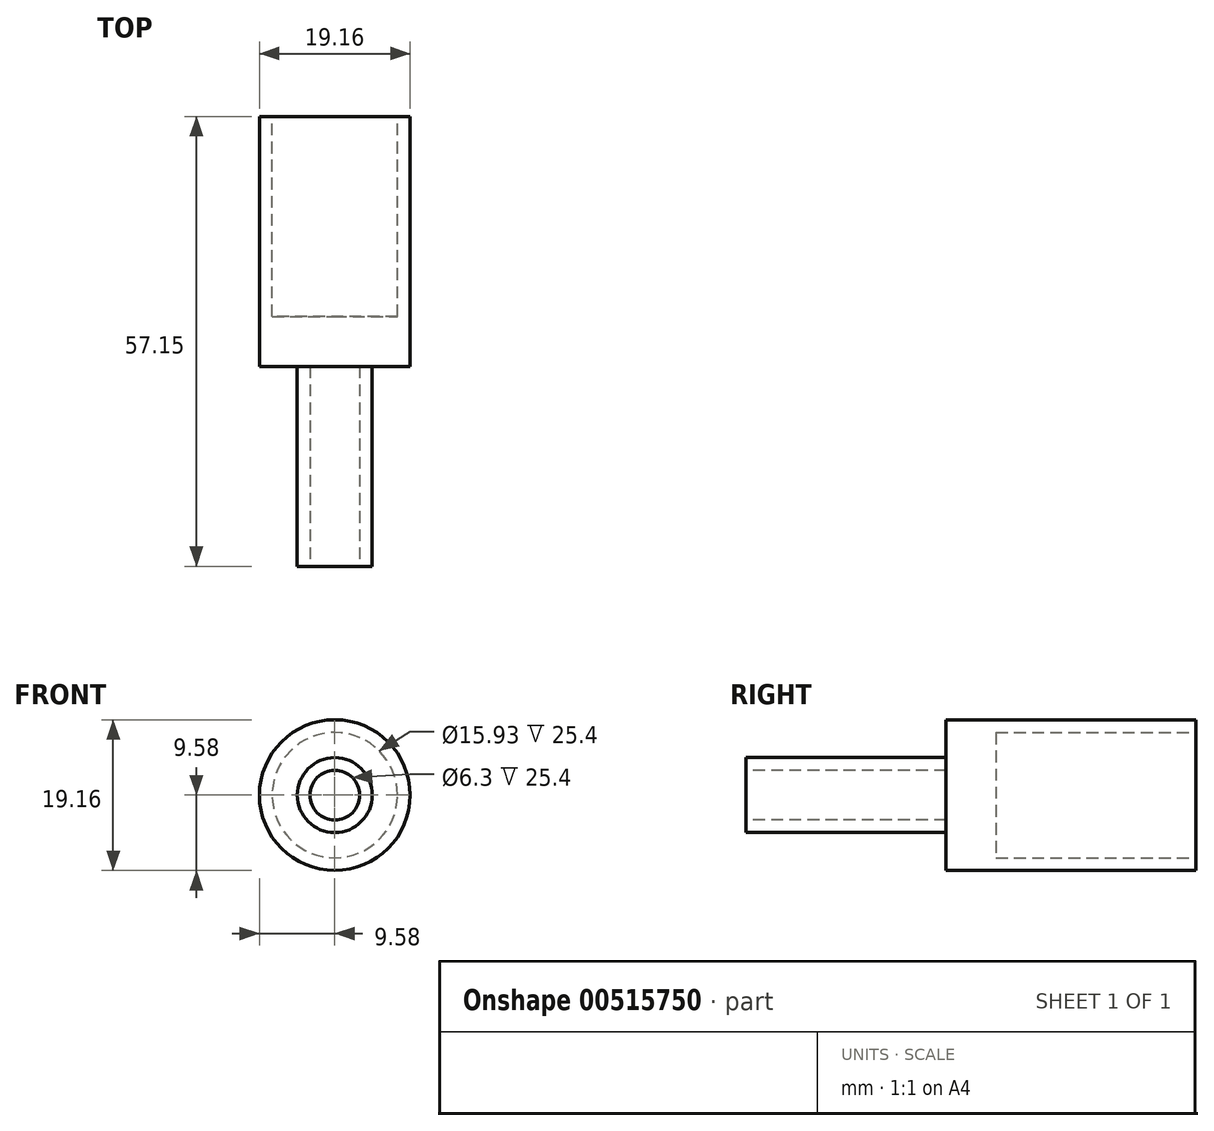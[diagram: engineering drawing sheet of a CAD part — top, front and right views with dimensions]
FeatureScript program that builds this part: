
annotation { "Feature Type Name" : "Feature", "Feature Type Description" : "" }
export const myFeature = defineFeature(function(context is Context, id is Id, definition is map)
    precondition{}
    {
        {
            var Q0;
            Q0=qCreatedBy(makeId("Front.planeOp"),FACE);
            var sketch = newSketch(context, id + "F0", { "sketchPlane" : qUnion([Q0])});
            skCircle(sketch, "E0", {"center": v(0, 0) * mm, "radius": 9.58 * mm});
            skSolve(sketch);
        }
        {
            var Q0;
            Q0=makeQuery(id+"F0.imprint","IMPRINT",FACE,{"disambiguationData":[TD([[makeQuery(id+"F0.imprint","IMPRINT",EDGE,{"derivedFrom":sQuery(id+"F0.wireOp",EDGE,"E0")}),1.0]])]});
            extrude(context, id + "F1", {"entities" : qUnion([Q0]), "oppositeDirection" : true, "depth" : 31.75 * mm, "offsetDistance" : 25.4 * mm});
        }
        {
            var Q0;
            Q0=makeQuery(id+"F1.opExtrude","CAP_FACE",FACE,{"disambiguationData":[OSD([sQuery(id+"F0.wireOp",EDGE,"E0")])],"isStart":false});
            var sketch = newSketch(context, id + "F2", { "sketchPlane" : qUnion([Q0])});
            skCircle(sketch, "E1", {"center": v(0, 0) * mm, "radius": 7.96 * mm});
            skSolve(sketch);
        }
        {
            var Q0;
            Q0=makeQuery(id+"F2.imprint","IMPRINT",FACE,{"disambiguationData":[TD([[makeQuery(id+"F2.imprint","IMPRINT",EDGE,{"derivedFrom":sQuery(id+"F2.wireOp",EDGE,"E1")}),1.0]])]});
            extrude(context, id + "F3", {"entities" : qUnion([Q0]), "operationType" : NewBodyOperationType.REMOVE, "oppositeDirection" : true, "depth" : 25.4 * mm, "offsetDistance" : 25.4 * mm});
        }
        {
            var Q0;
            Q0=makeQuery(id+"F1.opExtrude","CAP_FACE",FACE,{"disambiguationData":[OSD([sQuery(id+"F0.wireOp",EDGE,"E0")])],"isStart":true});
            var sketch = newSketch(context, id + "F4", { "sketchPlane" : qUnion([Q0])});
            skCircle(sketch, "E2", {"center": v(0, 0) * mm, "radius": 4.76 * mm});
            skSolve(sketch);
        }
        {
            var Q0;
            Q0=makeQuery(id+"F4.imprint","IMPRINT",FACE,{"disambiguationData":[TD([[makeQuery(id+"F4.imprint","IMPRINT",EDGE,{"derivedFrom":sQuery(id+"F4.wireOp",EDGE,"E2")}),1.0]])]});
            extrude(context, id + "F5", {"entities" : qUnion([Q0]), "operationType" : NewBodyOperationType.ADD, "depth" : 25.4 * mm, "offsetDistance" : 25.4 * mm});
        }
        {
            var Q0;
            Q0=makeQuery(id+"F5.opExtrude","CAP_FACE",FACE,{"disambiguationData":[OSD([sQuery(id+"F4.wireOp",EDGE,"E2")])],"isStart":false});
            var sketch = newSketch(context, id + "F6", { "sketchPlane" : qUnion([Q0])});
            skCircle(sketch, "E3", {"center": v(0, 0) * mm, "radius": 3.15 * mm});
            skSolve(sketch);
        }
        {
            var Q0;
            Q0=makeQuery(id+"F6.imprint","IMPRINT",FACE,{"disambiguationData":[TD([[makeQuery(id+"F6.imprint","IMPRINT",EDGE,{"derivedFrom":sQuery(id+"F6.wireOp",EDGE,"E3")}),1.0]])]});
            extrude(context, id + "F7", {"entities" : qUnion([Q0]), "operationType" : NewBodyOperationType.REMOVE, "oppositeDirection" : true, "depth" : 25.4 * mm, "offsetDistance" : 25.4 * mm});
        }
    });
